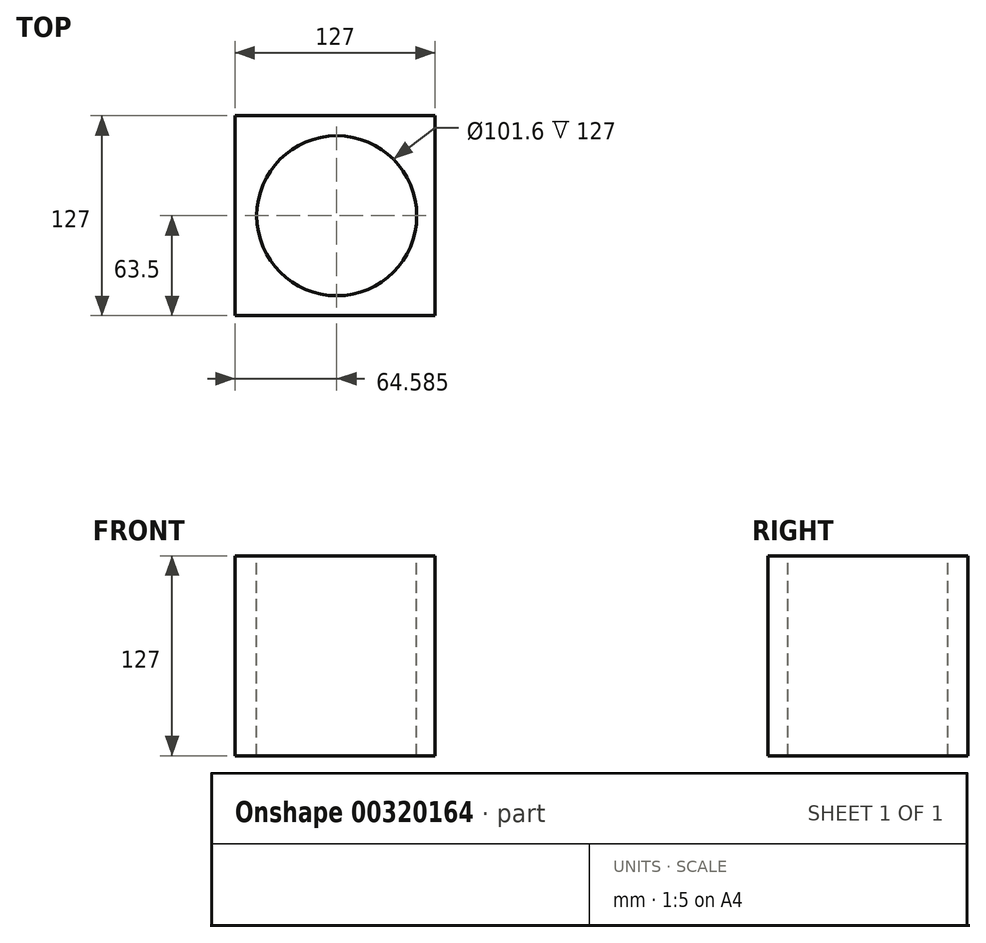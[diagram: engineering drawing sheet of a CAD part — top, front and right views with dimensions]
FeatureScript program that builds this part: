
annotation { "Feature Type Name" : "Feature", "Feature Type Description" : "" }
export const myFeature = defineFeature(function(context is Context, id is Id, definition is map)
    precondition{}
    {
        {
            var Q0;
            Q0=qCreatedBy(makeId("Top.planeOp"),FACE);
            var sketch = newSketch(context, id + "F0", { "sketchPlane" : qUnion([Q0])});
            skLineSegment(sketch, "E0.bottom", {"start": v(94.28, 63.5) * mm, "end": v(-32.72, 63.5) * mm});
            skLineSegment(sketch, "E0.top", {"start": v(94.28, -63.5) * mm, "end": v(-32.72, -63.5) * mm});
            skLineSegment(sketch, "E0.left", {"start": v(94.28, 63.5) * mm, "end": v(94.28, -63.5) * mm});
            skLineSegment(sketch, "E0.right", {"start": v(-32.72, 63.5) * mm, "end": v(-32.72, -63.5) * mm});
            skSolve(sketch);
        }
        {
            var Q0;
            Q0=makeQuery(id+"F0.imprint","IMPRINT",FACE,{"disambiguationData":[TD([[makeQuery(id+"F0.imprint","IMPRINT",EDGE,{"derivedFrom":sQuery(id+"F0.wireOp",EDGE,"E0.bottom")}),1.0]])]});
            var Q1;
            Q1=sQuery(id+"F0.wireOp",EDGE,"E0.left");
            var Q2;
            Q2=sQuery(id+"F0.wireOp",EDGE,"E0.bottom");
            var Q3;
            Q3=sQuery(id+"F0.wireOp",EDGE,"E0.right");
            var Q4;
            Q4=sQuery(id+"F0.wireOp",EDGE,"E0.top");
            extrude(context, id + "F1", {"entities" : qUnion([Q0]), "surfaceEntities" : qUnion([Q1, Q2, Q3, Q4]), "depth" : 127 * mm});
        }
        {
            var Q0;
            Q0=makeQuery(id+"F1.opExtrude","CAP_FACE",FACE,{"disambiguationData":[OSD([sQuery(id+"F0.wireOp",EDGE,"E0.bottom"),sQuery(id+"F0.wireOp",EDGE,"E0.top"),sQuery(id+"F0.wireOp",EDGE,"E0.left"),sQuery(id+"F0.wireOp",EDGE,"E0.right")])],"isStart":false});
            var sketch = newSketch(context, id + "F2", { "sketchPlane" : qUnion([Q0])});
            skLineSegment(sketch, "E1", {"start": v(94.28, 63.5) * mm, "end": v(-32.72, -63.5) * mm, "construction": true});
            skLineSegment(sketch, "E2", {"start": v(-32.72, -63.5) * mm, "end": v(-32.72, 63.5) * mm});
            skLineSegment(sketch, "E3", {"start": v(-32.72, 63.5) * mm, "end": v(94.28, -63.5) * mm, "construction": true});
            skSolve(sketch);
        }
        {
            var Q0;
            Q0=makeQuery(id+"F2.imprint","IMPRINT",FACE,{"disambiguationData":[TD([[makeQuery(id+"F2.imprint","IMPRINT",EDGE,{"derivedFrom":sQuery(id+"F2.wireOp",EDGE,"E2")}),1.0]])]});
            var sketch = newSketch(context, id + "F3", { "sketchPlane" : qUnion([Q0])});
            skCircle(sketch, "E4", {"center": v(31.86, 0) * mm, "radius": 50.8 * mm});
            skPoint(sketch, "E4.first.point", {"position": v(-18.94, 0) * mm});
            skPoint(sketch, "E4.second.point", {"position": v(64.77, 38.7) * mm});
            skPoint(sketch, "E4.third.point", {"position": v(75.5, 26) * mm});
            skSolve(sketch);
        }
        {
            var Q0;
            Q0=makeQuery(id+"F3.imprint","IMPRINT",FACE,{"disambiguationData":[TD([[makeQuery(id+"F3.imprint","IMPRINT",EDGE,{"derivedFrom":sQuery(id+"F3.wireOp",EDGE,"E4")}),1.0]])]});
            extrude(context, id + "F4", {"entities" : qUnion([Q0]), "operationType" : NewBodyOperationType.REMOVE, "oppositeDirection" : true, "depth" : 213.22 * mm});
        }
    });
